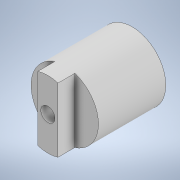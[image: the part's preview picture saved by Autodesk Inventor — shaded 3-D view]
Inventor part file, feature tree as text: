
AUTODESK INVENTOR PART (.ipt)
format: ipt  version: 2021 (Build 250183000, 183)  size: 109,056 bytes
history: native  units: in
note: dims shown in document units (in); Inventor stores cm internally (conversion verified against a paired STEP export)
features: sketch x2, extrude x2, hole x1
ambient origin geometry x8: Origin, YZ Plane, XZ Plane, XY Plane, X Axis, Y Axis, Z Axis, Center Point
bodies: Solid1 (feature_tree)
feature tree (5):
  sketch  "Sketch1"  dims[d0=0.7874in d1=0.7874in d2=0.0in]
  extrude  "Extrusion1"  Depth=0.7874in TaperAngle=0.0deg
  extrude  "Extrusion2"  Depth=0.2362in
  hole  "Hole1"  [1 undecoded]
  sketch  "Sketch2"  dims[d3=0.1181in d4=0.1181in d5=0.1969in d6=0.0in d7=0.1654in d8=0.2362in d9=0.1575in d10=0.0787in d11=90.0deg d12=0.315in d13=0.8108in]
note: 1 required parameter value undecoded (feature->parameter linkage not recoverable at this tier; creation-order binding heuristic only, values carry confidence <= 0.55)
